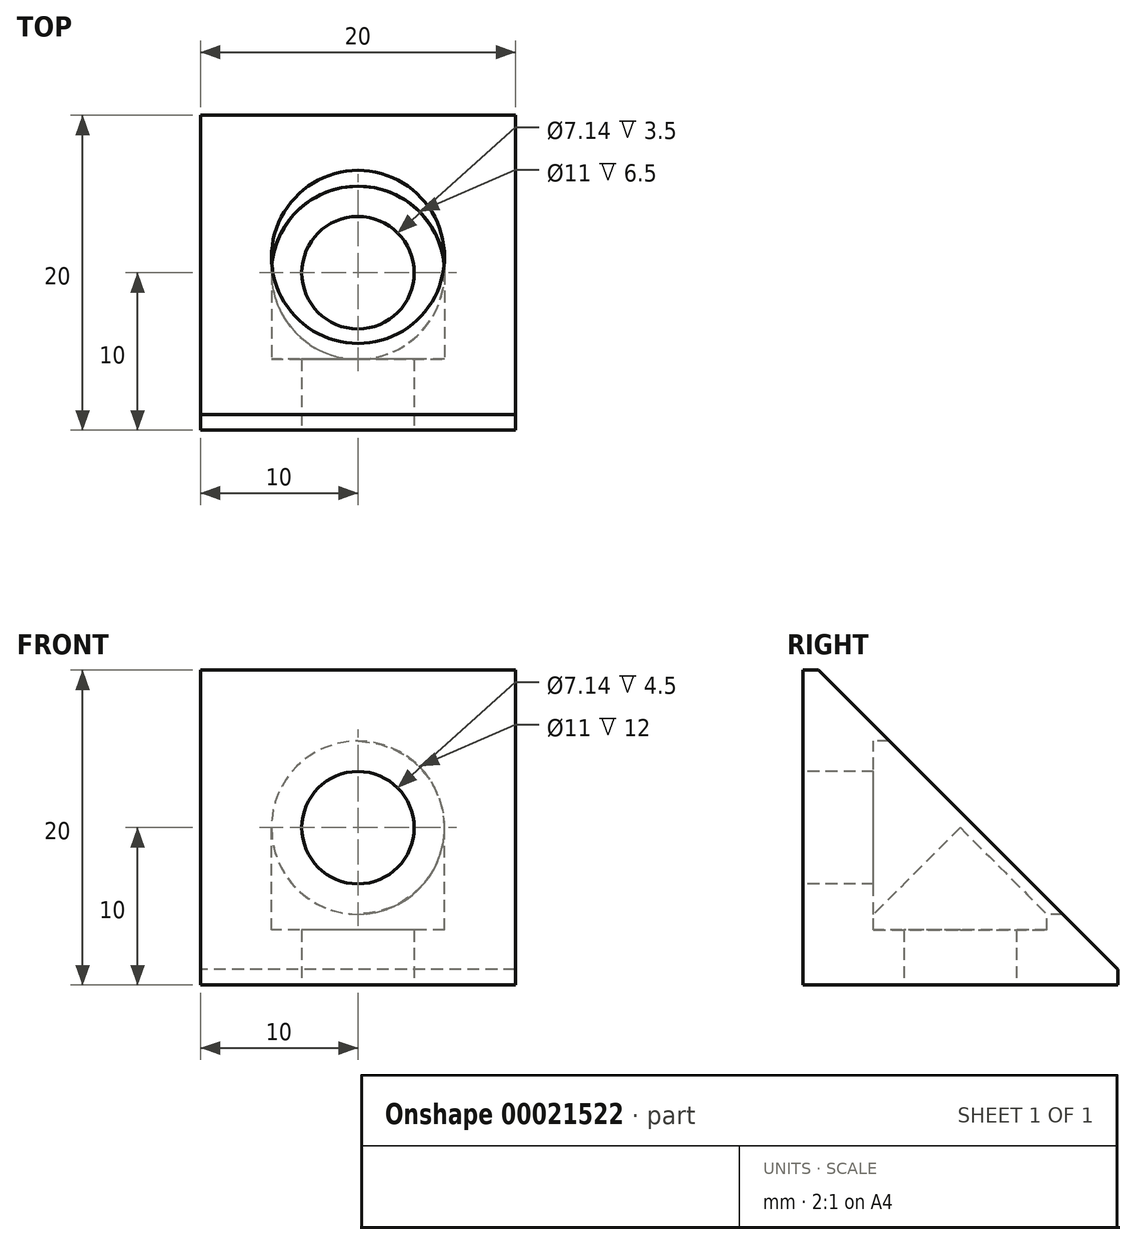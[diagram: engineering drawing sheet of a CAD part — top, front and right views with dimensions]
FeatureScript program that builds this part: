
annotation { "Feature Type Name" : "Feature", "Feature Type Description" : "" }
export const myFeature = defineFeature(function(context is Context, id is Id, definition is map)
    precondition{}
    {
        {
            var Q0;
            Q0=qCreatedBy(makeId("Right.planeOp"),FACE);
            var sketch = newSketch(context, id + "F0", { "sketchPlane" : qUnion([Q0])});
            skLineSegment(sketch, "E0.rect.bottom", {"start": v(-10, -10) * mm, "end": v(10, -10) * mm});
            skLineSegment(sketch, "E0.rect.top", {"start": v(-10, 10) * mm, "end": v(-9, 10) * mm});
            skLineSegment(sketch, "E0.rect.left", {"start": v(-10, -10) * mm, "end": v(-10, 10) * mm});
            skLineSegment(sketch, "E0.rect.right", {"start": v(10, -10) * mm, "end": v(10, -9) * mm});
            skPoint(sketch, "E0.rect.middle", {"position": v(0, 0) * mm});
            skLineSegment(sketch, "E1", {"start": v(-9, 10) * mm, "end": v(10, -9) * mm});
            skPoint(sketch, "E2.orphan", {"position": v(10, 10) * mm});
            skSolve(sketch);
        }
        {
            var Q0;
            Q0 = qSketchRegion(id + "F0", true);
            extrude(context, id + "F1", {"entities" : qUnion([Q0]), "endBound" : BoundingType.SYMMETRIC, "depth" : 20 * mm});
        }
        {
            var Q0;
            Q0=makeQuery(id+"F1.opExtrude","SWEPT_FACE",FACE,{"disambiguationData":[OSD([sQuery(id+"F0.wireOp",EDGE,"E0.rect.left")])]});
            var sketch = newSketch(context, id + "F2", { "sketchPlane" : qUnion([Q0])});
            skCircle(sketch, "E3", {"center": v(0, 0) * mm, "radius": 3.57 * mm});
            skSolve(sketch);
        }
        {
            var Q0;
            Q0=makeQuery(id+"F2.imprint","IMPRINT",FACE,{"disambiguationData":[TD([[makeQuery(id+"F2.imprint","IMPRINT",EDGE,{"derivedFrom":sQuery(id+"F2.wireOp",EDGE,"E3")}),1.0]])]});
            extrude(context, id + "F3", {"entities" : qUnion([Q0]), "operationType" : NewBodyOperationType.REMOVE, "oppositeDirection" : true, "depth" : 20 * mm});
        }
        {
            var Q0;
            Q0=qCreatedBy(makeId("Front.planeOp"),FACE);
            var sketch = newSketch(context, id + "F4", { "sketchPlane" : qUnion([Q0])});
            skCircle(sketch, "E4", {"center": v(0, 0) * mm, "radius": 5.5 * mm});
            skSolve(sketch);
        }
        {
            var Q0;
            Q0 = qSketchRegion(id + "F4", true);
            extrude(context, id + "F5", {"entities" : qUnion([Q0]), "operationType" : NewBodyOperationType.REMOVE, "endBound" : BoundingType.SYMMETRIC, "oppositeDirection" : true, "depth" : 11 * mm});
        }
        {
            var Q0;
            Q0=makeQuery(id+"F1.opExtrude","SWEPT_FACE",FACE,{"disambiguationData":[OSD([sQuery(id+"F0.wireOp",EDGE,"E0.rect.bottom")])]});
            var sketch = newSketch(context, id + "F6", { "sketchPlane" : qUnion([Q0])});
            skCircle(sketch, "E5", {"center": v(0, 0) * mm, "radius": 3.57 * mm});
            skSolve(sketch);
        }
        {
            var Q0;
            Q0 = qSketchRegion(id + "F6", true);
            extrude(context, id + "F7", {"entities" : qUnion([Q0]), "operationType" : NewBodyOperationType.REMOVE, "oppositeDirection" : true, "depth" : 20 * mm});
        }
        {
            var Q0;
            Q0=qCreatedBy(makeId("Top.planeOp"),FACE);
            var sketch = newSketch(context, id + "F8", { "sketchPlane" : qUnion([Q0])});
            skCircle(sketch, "E6", {"center": v(0, 0) * mm, "radius": 5.5 * mm});
            skSolve(sketch);
        }
        {
            var Q0;
            Q0 = qSketchRegion(id + "F8", true);
            extrude(context, id + "F9", {"entities" : qUnion([Q0]), "operationType" : NewBodyOperationType.REMOVE, "oppositeDirection" : true, "depth" : 6.5 * mm});
        }
        {
            var Q0;
            Q0=makeQuery(id+"F4.imprint","IMPRINT",FACE,{"disambiguationData":[TD([[makeQuery(id+"F4.imprint","IMPRINT",EDGE,{"derivedFrom":sQuery(id+"F4.wireOp",EDGE,"E4")}),1.0]])]});
            extrude(context, id + "F10", {"entities" : qUnion([Q0]), "operationType" : NewBodyOperationType.REMOVE, "oppositeDirection" : true, "depth" : 10 * mm});
        }
    });
